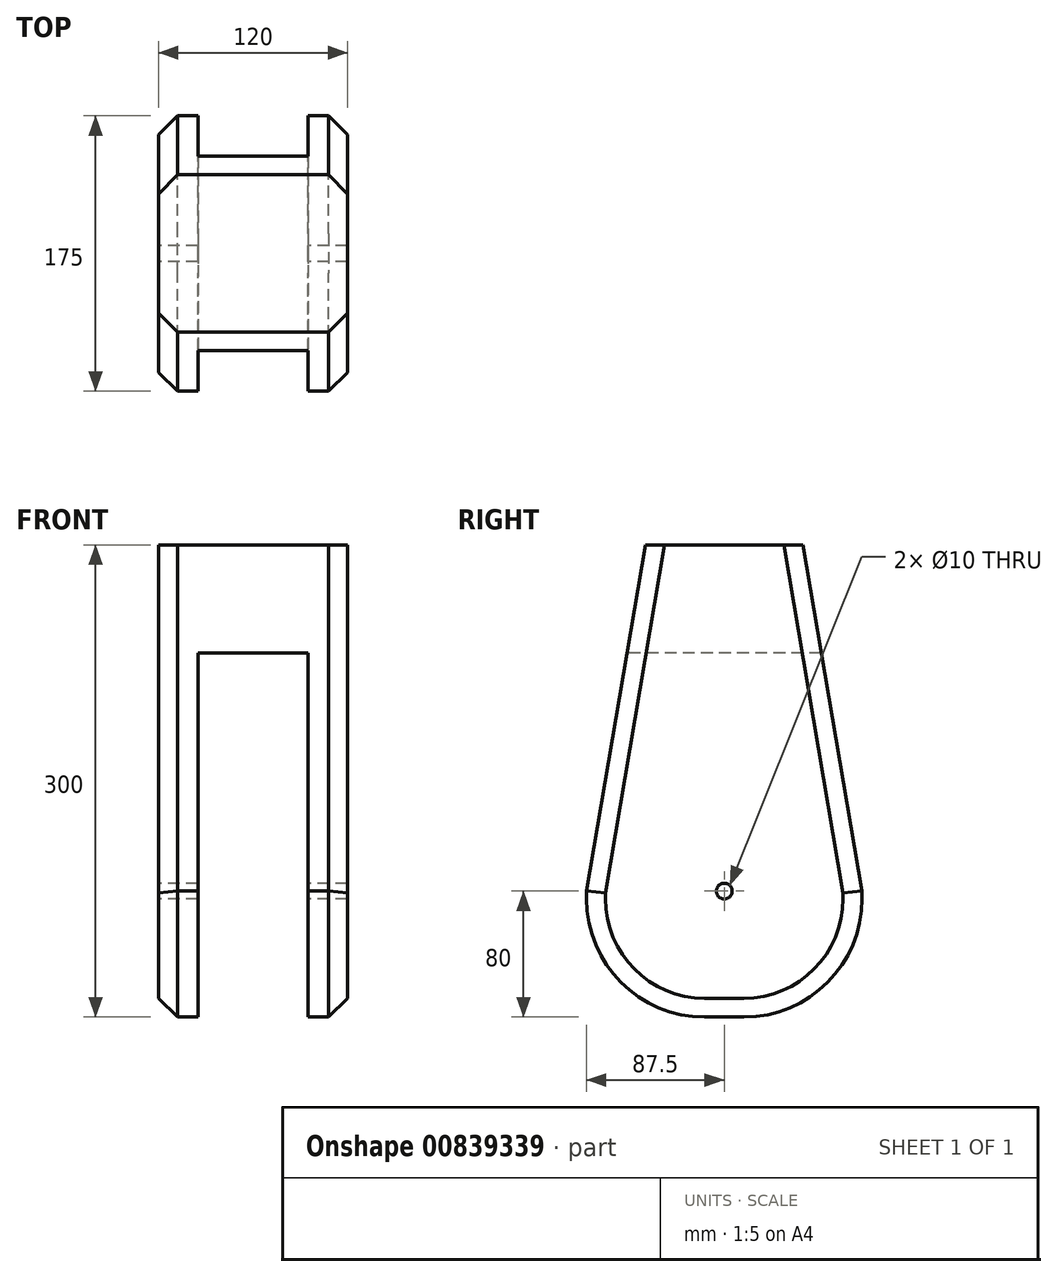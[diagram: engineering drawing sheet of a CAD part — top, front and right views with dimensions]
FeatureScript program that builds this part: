
annotation { "Feature Type Name" : "Feature", "Feature Type Description" : "" }
export const myFeature = defineFeature(function(context is Context, id is Id, definition is map)
    precondition{}
    {
        {
            var Q0;
            Q0=qCreatedBy(makeId("Right.planeOp"),FACE);
            var sketch = newSketch(context, id + "F0", { "sketchPlane" : qUnion([Q0])});
            skLineSegment(sketch, "E0", {"start": v(0, 455.61) * mm, "end": v(0, 200) * mm, "construction": true});
            skCircle(sketch, "E1", {"center": v(0, -90) * mm, "radius": 5 * mm});
            skLineSegment(sketch, "E2", {"start": v(-87.5, -170) * mm, "end": v(-87.5, -90) * mm});
            skPoint(sketch, "E3.start.orphan", {"position": v(-87.5, 0) * mm});
            skLineSegment(sketch, "E4.MirrorCS", {"start": v(87.5, -170) * mm, "end": v(87.5, -90) * mm});
            skPoint(sketch, "E5.MirrorCS.end.orphan", {"position": v(87.5, -170) * mm});
            skPoint(sketch, "E5.MirrorCS.start.orphan", {"position": v(87.5, 0) * mm});
            skLineSegment(sketch, "E6", {"start": v(87.5, -170) * mm, "end": v(-87.5, -170) * mm});
            skPoint(sketch, "E7.MirrorCS.start.orphan", {"position": v(0, -170) * mm});
            skLineSegment(sketch, "E8", {"start": v(-50, 130) * mm, "end": v(50, 130) * mm});
            skLineSegment(sketch, "E9.trimOffspring", {"start": v(0, 195) * mm, "end": v(0, -170) * mm, "construction": true});
            skPoint(sketch, "E10.center.orphan", {"position": v(0, 0) * mm});
            skLineSegment(sketch, "E11", {"start": v(50, 130) * mm, "end": v(87.5, -90) * mm});
            skLineSegment(sketch, "E12.MirrorCS", {"start": v(-50, 130) * mm, "end": v(-87.5, -90) * mm});
            skSolve(sketch);
        }
        {
            var Q0;
            Q0=makeQuery(id+"F0.imprint","IMPRINT",FACE,{"disambiguationData":[TD([[makeQuery(id+"F0.imprint","IMPRINT",EDGE,{"derivedFrom":sQuery(id+"F0.wireOp",EDGE,"bJJHOdsB-26hl-RVyC-n3W4-FHLlQgOHxvKo")}),1.0]])]});
            var Q1;
            Q1=makeQuery(id+"F0.imprint","IMPRINT",FACE,{"disambiguationData":[TD([[makeQuery(id+"F0.imprint","IMPRINT",EDGE,{"derivedFrom":sQuery(id+"F0.wireOp",EDGE,"RGSMXENa-Ee4u-1fXq-X1ao-Yd9uJYyGhcAm")}),1.0]])]});
            var Q2;
            Q2=makeQuery(id+"F0.imprint","IMPRINT",FACE,{"disambiguationData":[TD([[makeQuery(id+"F0.imprint","IMPRINT",EDGE,{"derivedFrom":sQuery(id+"F0.wireOp",EDGE,"E10")}),-1.0]])]});
            var Q3;
            Q3=makeQuery(id+"F0.imprint","IMPRINT",FACE,{"disambiguationData":[TD([[makeQuery(id+"F0.imprint","IMPRINT",EDGE,{"derivedFrom":sQuery(id+"F0.wireOp",EDGE,"E1")}),-1.0]])]});
            extrude(context, id + "F1", {"entities" : qUnion([Q0, Q1, Q2, Q3]), "endBound" : BoundingType.SYMMETRIC, "depth" : 120 * mm, "offsetDistance" : 25 * mm});
        }
        {
            var Q0;
            Q0=qCreatedBy(makeId("Right.planeOp"),FACE);
            var sketch = newSketch(context, id + "F2", { "sketchPlane" : qUnion([Q0])});
            skLineSegment(sketch, "E13.bottom", {"start": v(-176.38, 169.99) * mm, "end": v(129.62, 169.99) * mm});
            skLineSegment(sketch, "E13.top", {"start": v(-176.38, -136.01) * mm, "end": v(129.62, -136.01) * mm});
            skLineSegment(sketch, "E13.left", {"start": v(-176.38, 169.99) * mm, "end": v(-176.38, -136.01) * mm});
            skLineSegment(sketch, "E13.right", {"start": v(129.62, 169.99) * mm, "end": v(129.62, -136.01) * mm});
            skSolve(sketch);
        }
        {
            var Q0;
            Q0=makeQuery(id+"F2.imprint","IMPRINT",FACE,{"disambiguationData":[TD([[makeQuery(id+"F2.imprint","IMPRINT",EDGE,{"derivedFrom":sQuery(id+"F2.wireOp",EDGE,"E13.bottom")}),-1.0]])]});
            var sketch = newSketch(context, id + "F3", { "sketchPlane" : qUnion([Q0])});
            skLineSegment(sketch, "E14.bottom", {"start": v(108.1, 61.27) * mm, "end": v(-118.53, 61.27) * mm});
            skLineSegment(sketch, "E14.top", {"start": v(108.1, -195.48) * mm, "end": v(-118.53, -195.48) * mm});
            skLineSegment(sketch, "E14.left", {"start": v(108.1, 61.27) * mm, "end": v(108.1, -195.48) * mm});
            skLineSegment(sketch, "E14.right", {"start": v(-118.53, 61.27) * mm, "end": v(-118.53, -195.48) * mm});
            skSolve(sketch);
        }
        {
            var Q0;
            {var subQ0=sQuery(id+"F3.wireOp",EDGE,"E14.bottom");Q0=makeQuery(id+"F3.imprint","IMPRINT",FACE,{"disambiguationData":[TD([[makeQuery(id+"F3.imprint","IMPRINT",EDGE,{"derivedFrom":subQ0}),1.0]])]});}
            var Q1;
            {var subQ0=sQuery(id+"F3.wireOp",EDGE,"E14.top");Q1=makeQuery(id+"F3.imprint","IMPRINT",FACE,{"disambiguationData":[TD([[makeQuery(id+"F3.imprint","IMPRINT",EDGE,{"derivedFrom":subQ0}),-1.0]])]});}
            extrude(context, id + "F4", {"entities" : qUnion([Q0, Q1]), "operationType" : NewBodyOperationType.REMOVE, "endBound" : BoundingType.SYMMETRIC, "oppositeDirection" : true, "depth" : 70 * mm, "offsetDistance" : 25 * mm});
        }
        {
            var Q0;
            {var subQ0=sQuery(id+"F0.wireOp",EDGE,"E6");var subQ1=sQuery(id+"F0.wireOp",EDGE,"E2");Q0=makeQuery(id+"F4.boolean.opBoolean","SPLIT",EDGE,{"disambiguationData":[TD([makeQuery(id+"F4.opExtrude","CAP_FACE",FACE,{"disambiguationData":[OSD([sQuery(id+"FtQzms2HYuc1xRV_1.wireOp",EDGE,"bliS3hDE-CNeZ-lZ3X-Cnt4-Wg4Zo53HFOk7"),sQuery(id+"FtQzms2HYuc1xRV_1.wireOp",EDGE,"Ia10nzEQ-IUgD-dcOd-zplT-Xme1JM6c8USt"),sQuery(id+"FtQzms2HYuc1xRV_1.wireOp",EDGE,"Tf7FhkOn-U524-Fniq-BtrH-MYJQxx5zRe7X"),sQuery(id+"FtQzms2HYuc1xRV_1.wireOp",EDGE,"091fYJzw-RcpR-2AES-gSSs-nQW8jkHc21TU")])],"isStart":false})])],"derivedFrom":makeQuery(id+"F1.opExtrude","SWEPT_EDGE",EDGE,{"disambiguationData":[OSD([subQ1,subQ0])]})});}
            var Q1;
            {var subQ0=sQuery(id+"F0.wireOp",EDGE,"E6");var subQ1=sQuery(id+"F0.wireOp",EDGE,"E4.MirrorCS");Q1=makeQuery(id+"F4.boolean.opBoolean","SPLIT",EDGE,{"disambiguationData":[TD([makeQuery(id+"F4.opExtrude","CAP_FACE",FACE,{"disambiguationData":[OSD([sQuery(id+"FtQzms2HYuc1xRV_1.wireOp",EDGE,"bliS3hDE-CNeZ-lZ3X-Cnt4-Wg4Zo53HFOk7"),sQuery(id+"FtQzms2HYuc1xRV_1.wireOp",EDGE,"Ia10nzEQ-IUgD-dcOd-zplT-Xme1JM6c8USt"),sQuery(id+"FtQzms2HYuc1xRV_1.wireOp",EDGE,"Tf7FhkOn-U524-Fniq-BtrH-MYJQxx5zRe7X"),sQuery(id+"FtQzms2HYuc1xRV_1.wireOp",EDGE,"091fYJzw-RcpR-2AES-gSSs-nQW8jkHc21TU")])],"isStart":false})])],"derivedFrom":makeQuery(id+"F1.opExtrude","SWEPT_EDGE",EDGE,{"disambiguationData":[OSD([subQ1,subQ0])]})});}
            var Q2;
            {var subQ0=sQuery(id+"F0.wireOp",EDGE,"E6");var subQ1=sQuery(id+"F0.wireOp",EDGE,"E2");Q2=makeQuery(id+"F4.boolean.opBoolean","SPLIT",EDGE,{"disambiguationData":[TD([makeQuery(id+"F4.opExtrude","CAP_FACE",FACE,{"disambiguationData":[OSD([sQuery(id+"FtQzms2HYuc1xRV_1.wireOp",EDGE,"bliS3hDE-CNeZ-lZ3X-Cnt4-Wg4Zo53HFOk7"),sQuery(id+"FtQzms2HYuc1xRV_1.wireOp",EDGE,"Ia10nzEQ-IUgD-dcOd-zplT-Xme1JM6c8USt"),sQuery(id+"FtQzms2HYuc1xRV_1.wireOp",EDGE,"Tf7FhkOn-U524-Fniq-BtrH-MYJQxx5zRe7X"),sQuery(id+"FtQzms2HYuc1xRV_1.wireOp",EDGE,"091fYJzw-RcpR-2AES-gSSs-nQW8jkHc21TU")])],"isStart":true})])],"derivedFrom":makeQuery(id+"F1.opExtrude","SWEPT_EDGE",EDGE,{"disambiguationData":[OSD([subQ1,subQ0])]})});}
            var Q3;
            {var subQ0=sQuery(id+"F0.wireOp",EDGE,"E6");var subQ1=sQuery(id+"F0.wireOp",EDGE,"E4.MirrorCS");Q3=makeQuery(id+"F4.boolean.opBoolean","SPLIT",EDGE,{"disambiguationData":[TD([makeQuery(id+"F4.opExtrude","CAP_FACE",FACE,{"disambiguationData":[OSD([sQuery(id+"FtQzms2HYuc1xRV_1.wireOp",EDGE,"bliS3hDE-CNeZ-lZ3X-Cnt4-Wg4Zo53HFOk7"),sQuery(id+"FtQzms2HYuc1xRV_1.wireOp",EDGE,"Ia10nzEQ-IUgD-dcOd-zplT-Xme1JM6c8USt"),sQuery(id+"FtQzms2HYuc1xRV_1.wireOp",EDGE,"Tf7FhkOn-U524-Fniq-BtrH-MYJQxx5zRe7X"),sQuery(id+"FtQzms2HYuc1xRV_1.wireOp",EDGE,"091fYJzw-RcpR-2AES-gSSs-nQW8jkHc21TU")])],"isStart":true})])],"derivedFrom":makeQuery(id+"F1.opExtrude","SWEPT_EDGE",EDGE,{"disambiguationData":[OSD([subQ1,subQ0])]})});}
            var Q4;
            {var subQ0=sQuery(id+"F0.wireOp",EDGE,"E6");var subQ1=sQuery(id+"F0.wireOp",EDGE,"E4.MirrorCS");Q4=makeQuery(id+"F4.boolean.opBoolean","SPLIT",EDGE,{"disambiguationData":[TD([makeQuery(id+"F4.opExtrude","CAP_FACE",FACE,{"disambiguationData":[OSD([sQuery(id+"F3.wireOp",EDGE,"E14.bottom"),sQuery(id+"F3.wireOp",EDGE,"E14.top"),sQuery(id+"F3.wireOp",EDGE,"E14.left"),sQuery(id+"F3.wireOp",EDGE,"E14.right")])],"isStart":false})])],"derivedFrom":makeQuery(id+"F1.opExtrude","SWEPT_EDGE",EDGE,{"disambiguationData":[OSD([subQ1,subQ0])]})});}
            var Q5;
            {var subQ0=sQuery(id+"F0.wireOp",EDGE,"E6");var subQ1=sQuery(id+"F0.wireOp",EDGE,"E4.MirrorCS");Q5=makeQuery(id+"F4.boolean.opBoolean","SPLIT",EDGE,{"disambiguationData":[TD([makeQuery(id+"F4.opExtrude","CAP_FACE",FACE,{"disambiguationData":[OSD([sQuery(id+"F3.wireOp",EDGE,"E14.bottom"),sQuery(id+"F3.wireOp",EDGE,"E14.top"),sQuery(id+"F3.wireOp",EDGE,"E14.left"),sQuery(id+"F3.wireOp",EDGE,"E14.right")])],"isStart":true})])],"derivedFrom":makeQuery(id+"F1.opExtrude","SWEPT_EDGE",EDGE,{"disambiguationData":[OSD([subQ1,subQ0])]})});}
            var Q6;
            {var subQ0=sQuery(id+"F0.wireOp",EDGE,"E6");var subQ1=sQuery(id+"F0.wireOp",EDGE,"E2");Q6=makeQuery(id+"F4.boolean.opBoolean","SPLIT",EDGE,{"disambiguationData":[TD([makeQuery(id+"F4.opExtrude","CAP_FACE",FACE,{"disambiguationData":[OSD([sQuery(id+"F3.wireOp",EDGE,"E14.bottom"),sQuery(id+"F3.wireOp",EDGE,"E14.top"),sQuery(id+"F3.wireOp",EDGE,"E14.left"),sQuery(id+"F3.wireOp",EDGE,"E14.right")])],"isStart":true})])],"derivedFrom":makeQuery(id+"F1.opExtrude","SWEPT_EDGE",EDGE,{"disambiguationData":[OSD([subQ1,subQ0])]})});}
            var Q7;
            {var subQ0=sQuery(id+"F0.wireOp",EDGE,"E6");var subQ1=sQuery(id+"F0.wireOp",EDGE,"E2");Q7=makeQuery(id+"F4.boolean.opBoolean","SPLIT",EDGE,{"disambiguationData":[TD([makeQuery(id+"F4.opExtrude","CAP_FACE",FACE,{"disambiguationData":[OSD([sQuery(id+"F3.wireOp",EDGE,"E14.bottom"),sQuery(id+"F3.wireOp",EDGE,"E14.top"),sQuery(id+"F3.wireOp",EDGE,"E14.left"),sQuery(id+"F3.wireOp",EDGE,"E14.right")])],"isStart":false})])],"derivedFrom":makeQuery(id+"F1.opExtrude","SWEPT_EDGE",EDGE,{"disambiguationData":[OSD([subQ1,subQ0])]})});}
            fillet(context, id + "F5", {"entities" : qUnion([Q0, Q1, Q2, Q3, Q4, Q5, Q6, Q7]), "radius" : 75 * mm, "tangentPropagation" : true, "allowEdgeOverflow" : false});
        }
        {
            var Q0;
            Q0=makeQuery(id+"F1.opExtrude","CAP_EDGE",EDGE,{"disambiguationData":[OSD([sQuery(id+"F0.wireOp",EDGE,"E11")])],"isStart":false});
            var Q1;
            Q1=makeQuery(id+"F1.opExtrude","CAP_EDGE",EDGE,{"disambiguationData":[OSD([sQuery(id+"F0.wireOp",EDGE,"E11")])],"isStart":true});
            var Q2;
            {var subQ0=sQuery(id+"F0.wireOp",EDGE,"E6");var subQ1=sQuery(id+"F0.wireOp",EDGE,"E2");var subQ2=makeQuery(id+"F1.opExtrude","CAP_FACE",FACE,{"disambiguationData":[OSD([sQuery(id+"F0.wireOp",EDGE,"E1"),subQ1,sQuery(id+"F0.wireOp",EDGE,"E4.MirrorCS"),subQ0,sQuery(id+"F0.wireOp",EDGE,"E8"),sQuery(id+"F0.wireOp",EDGE,"E11"),sQuery(id+"F0.wireOp",EDGE,"E12.MirrorCS")])],"isStart":false});Q2=makeQuery(id+"F5.opFillet","BLEND_EDGE",EDGE,{"blendedFrom":[makeQuery(id+"F4.boolean.opBoolean","SPLIT",EDGE,{"disambiguationData":[TD([makeQuery(id+"F4.opExtrude","CAP_FACE",FACE,{"disambiguationData":[OSD([sQuery(id+"F3.wireOp",EDGE,"E14.bottom"),sQuery(id+"F3.wireOp",EDGE,"E14.top"),sQuery(id+"F3.wireOp",EDGE,"E14.left"),sQuery(id+"F3.wireOp",EDGE,"E14.right")])],"isStart":true})])],"derivedFrom":makeQuery(id+"F1.opExtrude","SWEPT_EDGE",EDGE,{"disambiguationData":[OSD([subQ1,subQ0])]})}),subQ2],"blendedInto":[subQ2]});}
            var Q3;
            Q3=makeQuery(id+"F1.opExtrude","CAP_EDGE",EDGE,{"disambiguationData":[OSD([sQuery(id+"F0.wireOp",EDGE,"E12.MirrorCS")])],"isStart":false});
            var Q4;
            {var subQ0=sQuery(id+"F0.wireOp",EDGE,"E6");var subQ1=sQuery(id+"F0.wireOp",EDGE,"E2");var subQ2=makeQuery(id+"F1.opExtrude","CAP_FACE",FACE,{"disambiguationData":[OSD([sQuery(id+"F0.wireOp",EDGE,"E1"),subQ1,sQuery(id+"F0.wireOp",EDGE,"E4.MirrorCS"),subQ0,sQuery(id+"F0.wireOp",EDGE,"E8"),sQuery(id+"F0.wireOp",EDGE,"E11"),sQuery(id+"F0.wireOp",EDGE,"E12.MirrorCS")])],"isStart":true});Q4=makeQuery(id+"F5.opFillet","BLEND_EDGE",EDGE,{"blendedFrom":[makeQuery(id+"F4.boolean.opBoolean","SPLIT",EDGE,{"disambiguationData":[TD([makeQuery(id+"F4.opExtrude","CAP_FACE",FACE,{"disambiguationData":[OSD([sQuery(id+"F3.wireOp",EDGE,"E14.bottom"),sQuery(id+"F3.wireOp",EDGE,"E14.top"),sQuery(id+"F3.wireOp",EDGE,"E14.left"),sQuery(id+"F3.wireOp",EDGE,"E14.right")])],"isStart":false})])],"derivedFrom":makeQuery(id+"F1.opExtrude","SWEPT_EDGE",EDGE,{"disambiguationData":[OSD([subQ1,subQ0])]})}),subQ2],"blendedInto":[subQ2]});}
            var Q5;
            Q5=makeQuery(id+"F1.opExtrude","CAP_EDGE",EDGE,{"disambiguationData":[OSD([sQuery(id+"F0.wireOp",EDGE,"E12.MirrorCS")])],"isStart":true});
            chamfer(context, id + "F6", {"entities" : qUnion([Q0, Q1, Q2, Q3, Q4, Q5]), "width" : 12 * mm, "tangentPropagation" : true});
        }
    });
